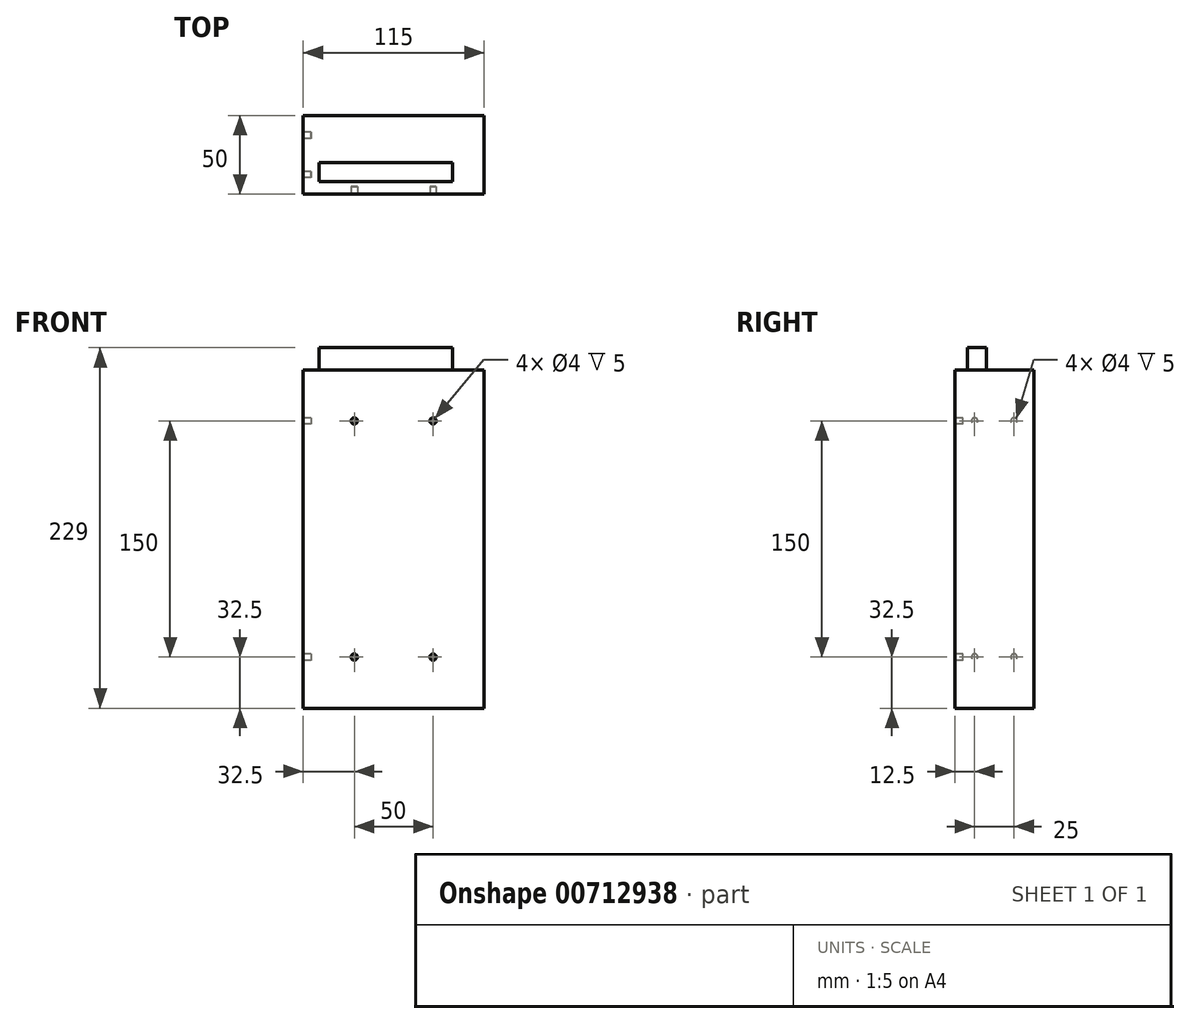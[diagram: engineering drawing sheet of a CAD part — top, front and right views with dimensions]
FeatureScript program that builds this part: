
annotation { "Feature Type Name" : "Feature", "Feature Type Description" : "" }
export const myFeature = defineFeature(function(context is Context, id is Id, definition is map)
    precondition{}
    {
        {
            var Q0;
            Q0=qCreatedBy(makeId("Front.planeOp"),FACE);
            var sketch = newSketch(context, id + "F0", { "sketchPlane" : qUnion([Q0])});
            skLineSegment(sketch, "E0.bottom", {"start": v(0, 0) * mm, "end": v(115, 0) * mm});
            skLineSegment(sketch, "E0.top", {"start": v(0, 215) * mm, "end": v(115, 215) * mm});
            skLineSegment(sketch, "E0.left", {"start": v(0, 0) * mm, "end": v(0, 215) * mm});
            skLineSegment(sketch, "E0.right", {"start": v(115, 0) * mm, "end": v(115, 215) * mm});
            skSolve(sketch);
        }
        {
            var Q0;
            Q0=makeQuery(id+"F0.imprint","IMPRINT",FACE,{"disambiguationData":[TD([[makeQuery(id+"F0.imprint","IMPRINT",EDGE,{"derivedFrom":sQuery(id+"F0.wireOp",EDGE,"E0.bottom")}),1.0]])]});
            extrude(context, id + "F1", {"entities" : qUnion([Q0]), "depth" : 50 * mm, "offsetDistance" : 25 * mm});
        }
        {
            var Q0;
            Q0=makeQuery(id+"F1.opExtrude","SWEPT_FACE",FACE,{"disambiguationData":[OSD([sQuery(id+"F0.wireOp",EDGE,"E0.top")])]});
            var sketch = newSketch(context, id + "F2", { "sketchPlane" : qUnion([Q0])});
            skLineSegment(sketch, "E1.bottom", {"start": v(10, -30) * mm, "end": v(95, -30) * mm});
            skLineSegment(sketch, "E1.top", {"start": v(10, -42) * mm, "end": v(95, -42) * mm});
            skLineSegment(sketch, "E1.left", {"start": v(10, -30) * mm, "end": v(10, -42) * mm});
            skLineSegment(sketch, "E1.right", {"start": v(95, -30) * mm, "end": v(95, -42) * mm});
            skSolve(sketch);
        }
        {
            var Q0;
            Q0=makeQuery(id+"F2.imprint","IMPRINT",FACE,{"disambiguationData":[TD([[makeQuery(id+"F2.imprint","IMPRINT",EDGE,{"derivedFrom":sQuery(id+"F2.wireOp",EDGE,"E1.bottom")}),-1.0]])]});
            extrude(context, id + "F3", {"entities" : qUnion([Q0]), "operationType" : NewBodyOperationType.ADD, "depth" : 14 * mm, "offsetDistance" : 25 * mm});
        }
        {
            var Q0;
            Q0=makeQuery(id+"F1.opExtrude","CAP_FACE",FACE,{"disambiguationData":[OSD([sQuery(id+"F0.wireOp",EDGE,"E0.bottom"),sQuery(id+"F0.wireOp",EDGE,"E0.top"),sQuery(id+"F0.wireOp",EDGE,"E0.left"),sQuery(id+"F0.wireOp",EDGE,"E0.right")])],"isStart":false});
            var sketch = newSketch(context, id + "F4", { "sketchPlane" : qUnion([Q0])});
            skLineSegment(sketch, "E2", {"start": v(57.5, 215) * mm, "end": v(57.5, 32.5) * mm, "construction": true});
            skLineSegment(sketch, "E3.bottom", {"start": v(32.5, 182.5) * mm, "end": v(82.5, 182.5) * mm, "construction": true});
            skLineSegment(sketch, "E3.top", {"start": v(32.5, 32.5) * mm, "end": v(82.5, 32.5) * mm, "construction": true});
            skLineSegment(sketch, "E3.left", {"start": v(32.5, 182.5) * mm, "end": v(32.5, 32.5) * mm, "construction": true});
            skLineSegment(sketch, "E3.right", {"start": v(82.5, 182.5) * mm, "end": v(82.5, 32.5) * mm, "construction": true});
            skCircle(sketch, "E4", {"center": v(32.5, 182.5) * mm, "radius": 2 * mm});
            skCircle(sketch, "E5", {"center": v(82.5, 182.5) * mm, "radius": 2 * mm});
            skCircle(sketch, "E6", {"center": v(82.5, 32.5) * mm, "radius": 2 * mm});
            skCircle(sketch, "E7", {"center": v(32.5, 32.5) * mm, "radius": 2 * mm});
            skSolve(sketch);
        }
        {
            var Q0;
            Q0 = qSketchRegion(id + "F4", true);
            extrude(context, id + "F5", {"entities" : qUnion([Q0]), "operationType" : NewBodyOperationType.REMOVE, "oppositeDirection" : true, "depth" : 5 * mm, "offsetDistance" : 25 * mm});
        }
        {
            var Q0;
            Q0=makeQuery(id+"F1.opExtrude","SWEPT_FACE",FACE,{"disambiguationData":[OSD([sQuery(id+"F0.wireOp",EDGE,"E0.left")])]});
            var sketch = newSketch(context, id + "F6", { "sketchPlane" : qUnion([Q0])});
            skLineSegment(sketch, "E8", {"start": v(25, 215) * mm, "end": v(25, 189.6) * mm, "construction": true});
            skLineSegment(sketch, "E9", {"start": v(50, 107.5) * mm, "end": v(38.62, 107.5) * mm, "construction": true});
            skCircle(sketch, "E10", {"center": v(12.5, 182.5) * mm, "radius": 2 * mm});
            skCircle(sketch, "E11.MirrorC", {"center": v(37.5, 182.5) * mm, "radius": 2 * mm});
            skCircle(sketch, "E12.MirrorC", {"center": v(37.5, 32.5) * mm, "radius": 2 * mm});
            skCircle(sketch, "E13.MirrorC", {"center": v(12.5, 32.5) * mm, "radius": 2 * mm});
            skSolve(sketch);
        }
        {
            var Q0;
            Q0 = qSketchRegion(id + "F6", true);
            extrude(context, id + "F7", {"entities" : qUnion([Q0]), "operationType" : NewBodyOperationType.REMOVE, "oppositeDirection" : true, "depth" : 5 * mm, "offsetDistance" : 25 * mm});
        }
    });
